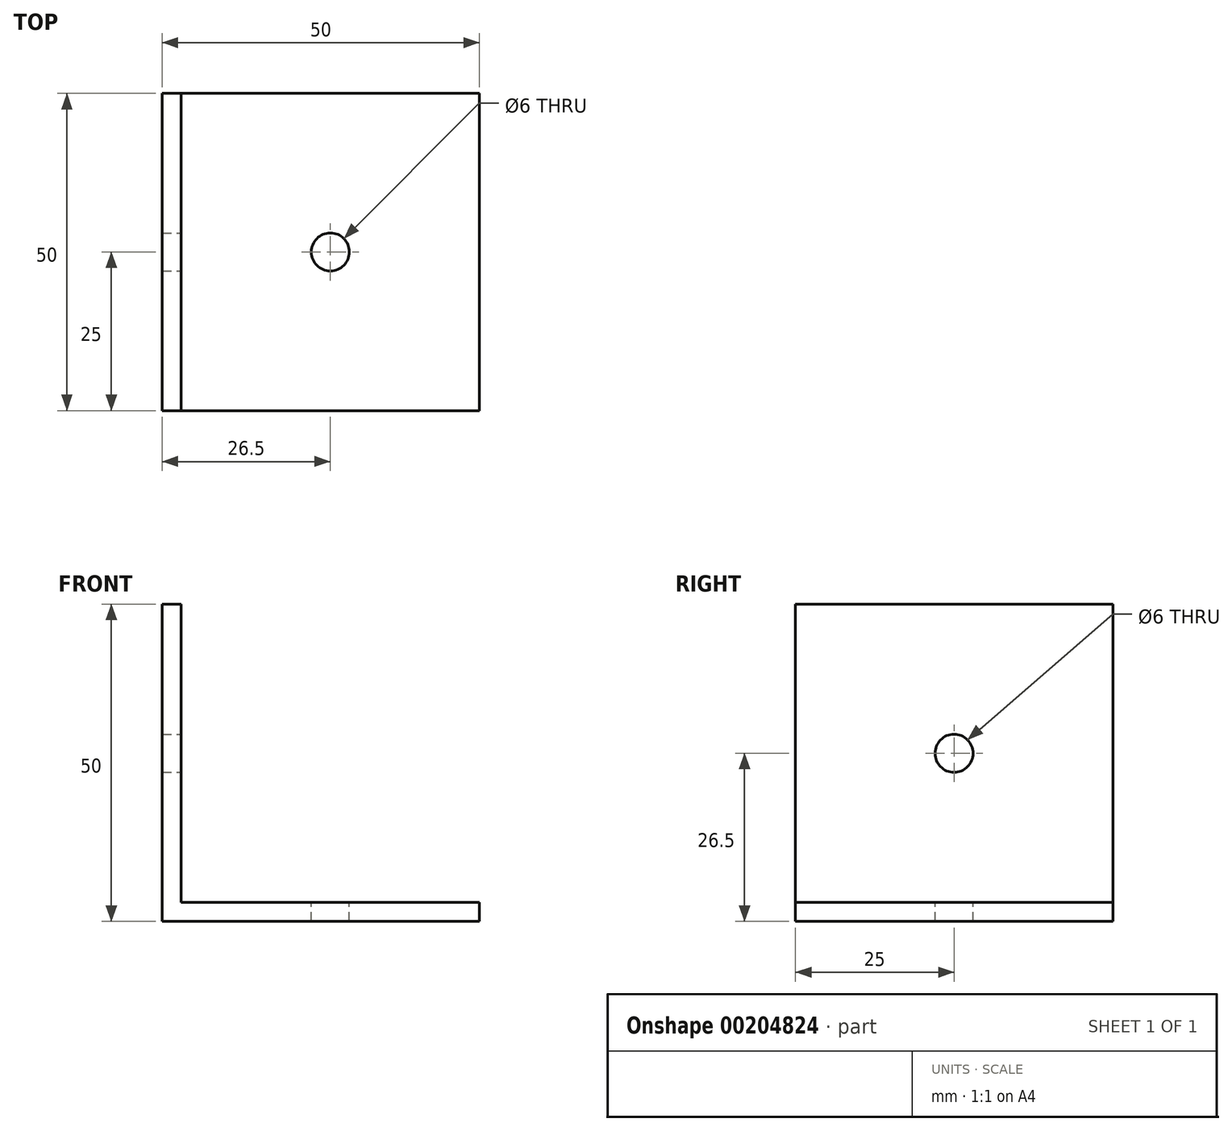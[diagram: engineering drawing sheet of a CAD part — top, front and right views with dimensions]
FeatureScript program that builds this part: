
annotation { "Feature Type Name" : "Feature", "Feature Type Description" : "" }
export const myFeature = defineFeature(function(context is Context, id is Id, definition is map)
    precondition{}
    {
        {
            var Q0;
            Q0=qCreatedBy(makeId("Front.planeOp"),FACE);
            var sketch = newSketch(context, id + "F0", { "sketchPlane" : qUnion([Q0])});
            skLineSegment(sketch, "E0", {"start": v(0, 0) * mm, "end": v(0, 50) * mm});
            skLineSegment(sketch, "E1", {"start": v(0, 50) * mm, "end": v(3, 50) * mm});
            skLineSegment(sketch, "E2", {"start": v(3, 50) * mm, "end": v(3, 3) * mm});
            skLineSegment(sketch, "E3", {"start": v(3, 3) * mm, "end": v(50, 3) * mm});
            skLineSegment(sketch, "E4", {"start": v(50, 3) * mm, "end": v(50, 0) * mm});
            skLineSegment(sketch, "E5", {"start": v(50, 0) * mm, "end": v(0, 0) * mm});
            skSolve(sketch);
        }
        {
            var Q0;
            Q0=makeQuery(id+"F0.imprint","IMPRINT",FACE,{"disambiguationData":[TD([[makeQuery(id+"F0.imprint","IMPRINT",EDGE,{"derivedFrom":sQuery(id+"F0.wireOp",EDGE,"E0")}),-1.0]])]});
            extrude(context, id + "F1", {"entities" : qUnion([Q0]), "depth" : 50 * mm});
        }
        {
            var Q0;
            Q0=makeQuery(id+"F1.opExtrude","SWEPT_FACE",FACE,{"disambiguationData":[OSD([sQuery(id+"F0.wireOp",EDGE,"E2")])]});
            var sketch = newSketch(context, id + "F2", { "sketchPlane" : qUnion([Q0])});
            skCircle(sketch, "E6", {"center": v(-25, 26.5) * mm, "radius": 3 * mm});
            skSolve(sketch);
        }
        {
            var Q0;
            Q0=makeQuery(id+"F2.imprint","IMPRINT",FACE,{"disambiguationData":[TD([[makeQuery(id+"F2.imprint","IMPRINT",EDGE,{"derivedFrom":sQuery(id+"F2.wireOp",EDGE,"E6")}),1.0]])]});
            extrude(context, id + "F3", {"entities" : qUnion([Q0]), "operationType" : NewBodyOperationType.REMOVE, "endBound" : BoundingType.UP_TO_NEXT, "oppositeDirection" : true, "depth" : 25 * mm});
        }
        {
            var Q0;
            Q0=makeQuery(id+"F1.opExtrude","SWEPT_FACE",FACE,{"disambiguationData":[OSD([sQuery(id+"F0.wireOp",EDGE,"E3")])]});
            var sketch = newSketch(context, id + "F4", { "sketchPlane" : qUnion([Q0])});
            skCircle(sketch, "E7", {"center": v(26.5, -25) * mm, "radius": 3 * mm});
            skSolve(sketch);
        }
        {
            var Q0;
            Q0=makeQuery(id+"F4.imprint","IMPRINT",FACE,{"disambiguationData":[TD([[makeQuery(id+"F4.imprint","IMPRINT",EDGE,{"derivedFrom":sQuery(id+"F4.wireOp",EDGE,"E7")}),1.0]])]});
            extrude(context, id + "F5", {"entities" : qUnion([Q0]), "operationType" : NewBodyOperationType.REMOVE, "endBound" : BoundingType.THROUGH_ALL, "oppositeDirection" : true, "depth" : 25 * mm});
        }
    });
